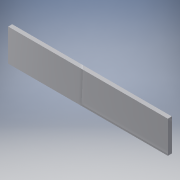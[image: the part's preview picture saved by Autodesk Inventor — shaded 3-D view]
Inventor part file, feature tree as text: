
AUTODESK INVENTOR PART (.ipt)
format: ipt  version: 2016 (Build 200138000, 138)  size: 102,400 bytes
history: native  units: in
note: dims shown in document units (in); Inventor stores cm internally (conversion verified against a paired STEP export)
features: extrude x2, sketch x2
ambient origin geometry x8: Origin, YZ Plane, XZ Plane, XY Plane, X Axis, Y Axis, Z Axis, Center Point
bodies: Solid1 (feature_tree)
feature tree (4):
  extrude  "Extrusion1"  Depth=1.0in
  extrude  "Extrusion2"  Depth=0.125in
  sketch  "Sketch1"  dims[d0=4.975in d1=1.0in]
  sketch  "Sketch2"  dims[d2=0.125in d3=0.0in d4=0.2656in d5=0.5in d6=0.5in d7=1.0in d8=0.5in d9=0.125in d10=0.0in]
